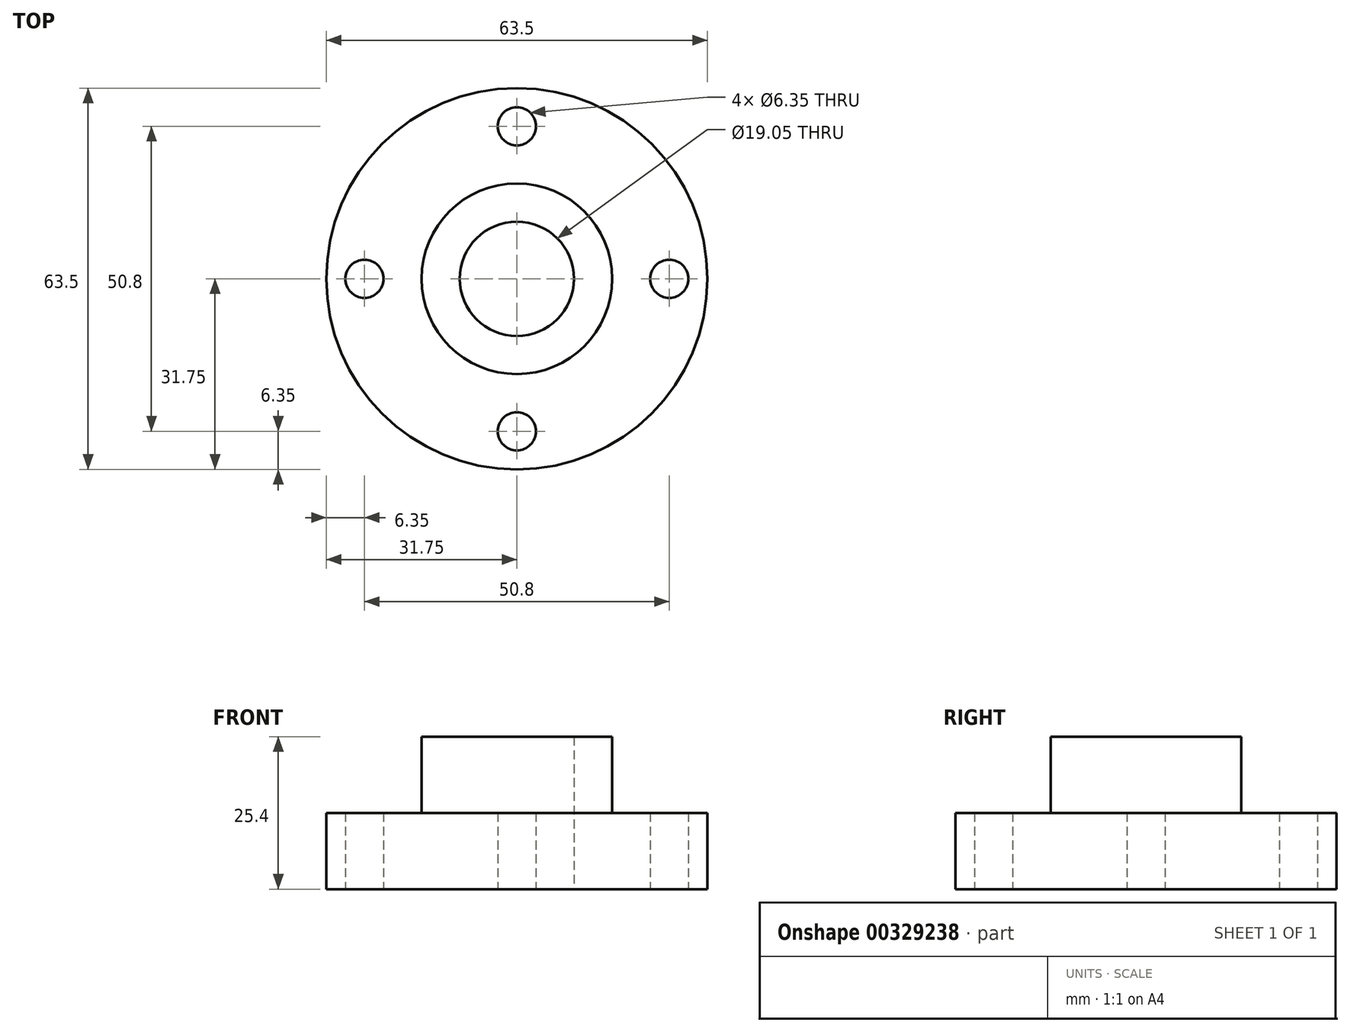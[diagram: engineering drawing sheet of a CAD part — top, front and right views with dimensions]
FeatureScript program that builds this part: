
annotation { "Feature Type Name" : "Feature", "Feature Type Description" : "" }
export const myFeature = defineFeature(function(context is Context, id is Id, definition is map)
    precondition{}
    {
        {
            var Q0;
            Q0=qCreatedBy(makeId("Top.planeOp"),FACE);
            var sketch = newSketch(context, id + "F0", { "sketchPlane" : qUnion([Q0])});
            skCircle(sketch, "E0", {"center": v(0, 0) * mm, "radius": 9.53 * mm});
            skCircle(sketch, "E1", {"center": v(0, 0) * mm, "radius": 15.88 * mm});
            skCircle(sketch, "E2", {"center": v(0, 0) * mm, "radius": 25.4 * mm, "construction": true});
            skCircle(sketch, "E3", {"center": v(0, 0) * mm, "radius": 31.75 * mm});
            skLineSegment(sketch, "E4", {"start": v(-31.75, 0) * mm, "end": v(31.75, 0) * mm, "construction": true});
            skLineSegment(sketch, "E5", {"start": v(0, 31.75) * mm, "end": v(0, -31.75) * mm, "construction": true});
            skCircle(sketch, "E6", {"center": v(0, 25.4) * mm, "radius": 3.18 * mm});
            skCircle(sketch, "E7", {"center": v(25.4, 0) * mm, "radius": 3.18 * mm});
            skCircle(sketch, "E8", {"center": v(0, -25.4) * mm, "radius": 3.18 * mm});
            skCircle(sketch, "E9", {"center": v(-25.4, 0) * mm, "radius": 3.18 * mm});
            skSolve(sketch);
        }
        {
            var Q0;
            Q0=makeQuery(id+"F0.imprint","IMPRINT",FACE,{"disambiguationData":[TD([[makeQuery(id+"F0.imprint","IMPRINT",EDGE,{"derivedFrom":sQuery(id+"F0.wireOp",EDGE,"E1")}),-1.0]])]});
            extrude(context, id + "F1", {"entities" : qUnion([Q0]), "depth" : 12.7 * mm});
        }
        {
            var Q0;
            Q0=makeQuery(id+"F0.imprint","IMPRINT",FACE,{"disambiguationData":[TD([[makeQuery(id+"F0.imprint","IMPRINT",EDGE,{"derivedFrom":sQuery(id+"F0.wireOp",EDGE,"E0")}),-1.0]])]});
            extrude(context, id + "F2", {"entities" : qUnion([Q0]), "operationType" : NewBodyOperationType.ADD, "depth" : 25.4 * mm});
        }
    });
